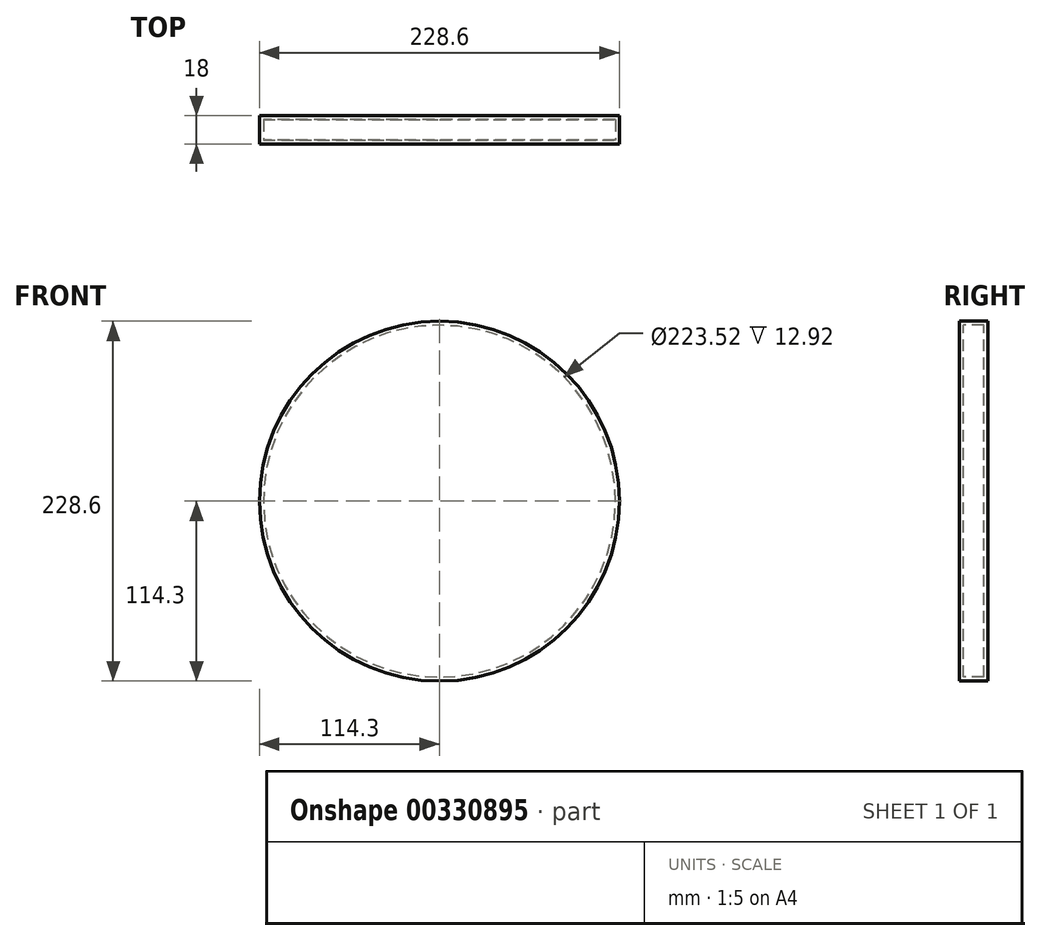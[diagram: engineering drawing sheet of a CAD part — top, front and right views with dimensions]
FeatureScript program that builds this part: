
annotation { "Feature Type Name" : "Feature", "Feature Type Description" : "" }
export const myFeature = defineFeature(function(context is Context, id is Id, definition is map)
    precondition{}
    {
        {
            assignVariable(context, id + "F0", {"name" : "r", "anyValue" : 9});
        }
        {
            var Q0;
            Q0=qCreatedBy(makeId("Front.planeOp"),FACE);
            var sketch = newSketch(context, id + "F1", { "sketchPlane" : qUnion([Q0])});
            skCircle(sketch, "E0", {"center": v(0, 0) * mm, "radius": 114.3 * mm});
            skSolve(sketch);
        }
        {
            var Q0;
            Q0=makeQuery(id+"F1.imprint","IMPRINT",FACE,{"disambiguationData":[TD([[makeQuery(id+"F1.imprint","IMPRINT",EDGE,{"derivedFrom":sQuery(id+"F1.wireOp",EDGE,"E0")}),1.0]])]});
            extrude(context, id + "F2", {"entities" : qUnion([Q0]), "oppositeDirection" : true, "depth" : (getVariable(context, 'r') * 2) * mm, "offsetDistance" : 25.4 * mm});
        }
        {
            var Q0;
            Q0=makeQuery(id+"F2.opExtrude","CAP_FACE",FACE,{"disambiguationData":[OSD([sQuery(id+"F1.wireOp",EDGE,"E0")])],"isStart":true});
            var Q1;
            Q1=makeQuery(id+"F2.opExtrude","CAP_FACE",FACE,{"disambiguationData":[OSD([sQuery(id+"F1.wireOp",EDGE,"E0")])],"isStart":false});
            var Q2;
            Q2=makeQuery(id+"F2.opExtrude","SWEPT_BODY",BODY,{"disambiguationData":[OSD([sQuery(id+"F1.wireOp",EDGE,"E0")])]});
            shell(context, id + "F3", {"isHollow" : true, "entities" : qUnion([Q0, Q1]), "parts" : qUnion([Q2]), "thickness" : 2.54 * mm});
        }
    });
